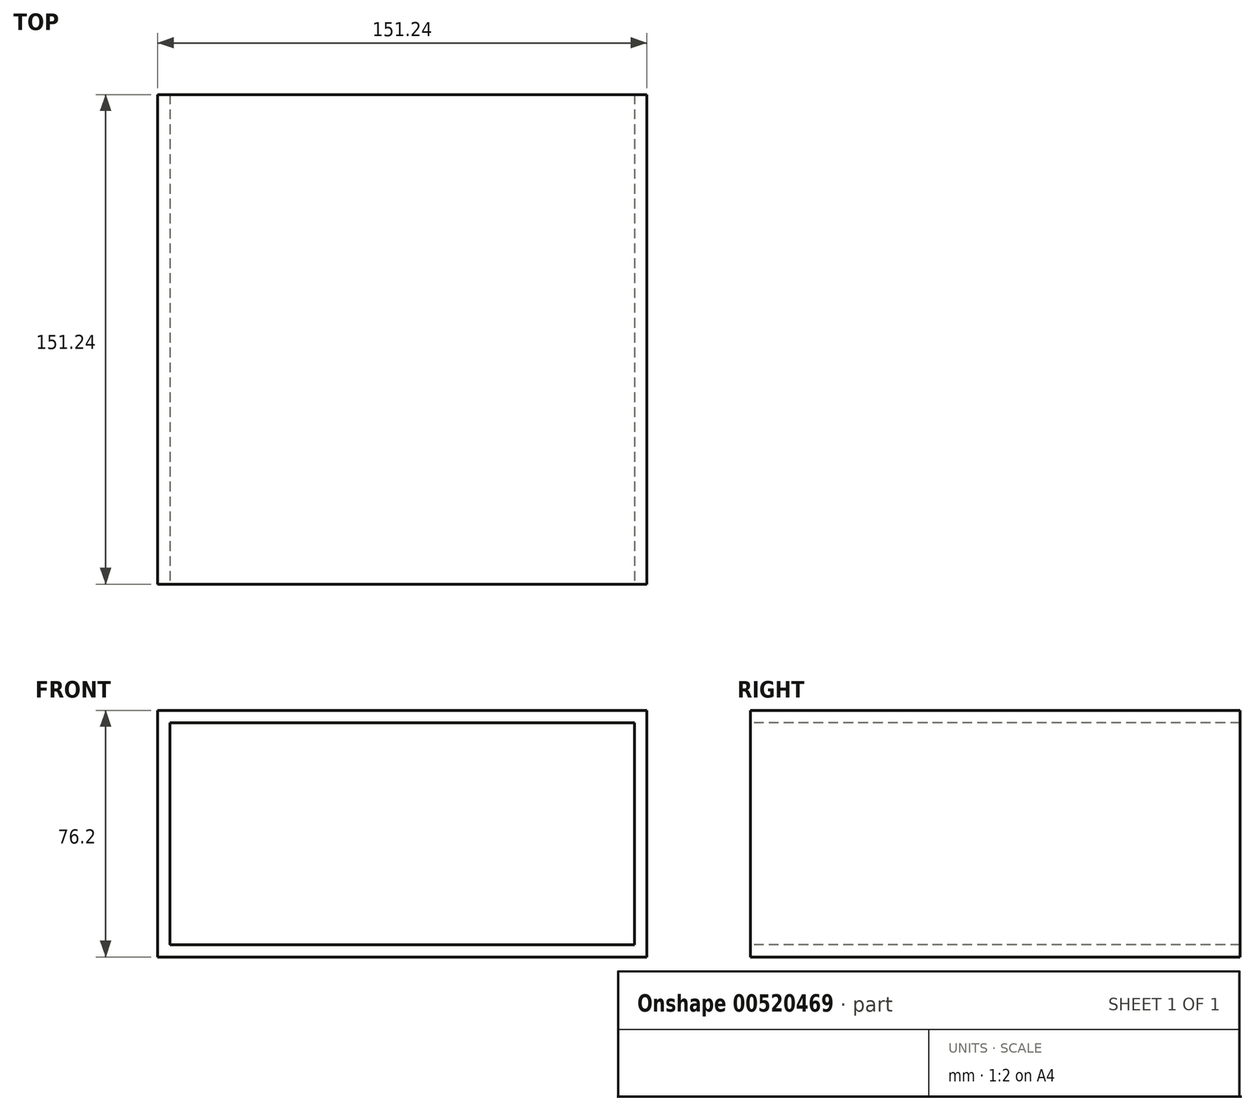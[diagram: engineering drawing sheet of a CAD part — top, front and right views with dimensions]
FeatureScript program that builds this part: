
annotation { "Feature Type Name" : "Feature", "Feature Type Description" : "" }
export const myFeature = defineFeature(function(context is Context, id is Id, definition is map)
    precondition{}
    {
        {
            var Q0;
            Q0=qCreatedBy(makeId("Top.planeOp"),FACE);
            var sketch = newSketch(context, id + "F0", { "sketchPlane" : qUnion([Q0])});
            skCircle(sketch, "E0.cCircle", {"center": v(0, 0) * mm, "radius": 75.62 * mm, "construction": true});
            skLineSegment(sketch, "E0.0", {"start": v(75.62, 75.62) * mm, "end": v(75.62, -75.62) * mm});
            skLineSegment(sketch, "E0.1", {"start": v(75.62, -75.62) * mm, "end": v(-75.62, -75.62) * mm});
            skLineSegment(sketch, "E0.2", {"start": v(-75.62, -75.62) * mm, "end": v(-75.62, 75.62) * mm});
            skLineSegment(sketch, "E0.3", {"start": v(-75.62, 75.62) * mm, "end": v(75.62, 75.62) * mm});
            skPoint(sketch, "E0.0.midPoint", {"position": v(75.62, 0) * mm});
            skSolve(sketch);
        }
        {
            var Q0;
            Q0 = qSketchRegion(id + "F0", true);
            extrude(context, id + "F1", {"entities" : qUnion([Q0]), "depth" : 76.2 * mm, "offsetDistance" : 25.4 * mm});
        }
        {
            var Q0;
            Q0=makeQuery(id+"F1.opExtrude","SWEPT_FACE",FACE,{"disambiguationData":[OSD([sQuery(id+"F0.wireOp",EDGE,"E0.1")])]});
            var sketch = newSketch(context, id + "F2", { "sketchPlane" : qUnion([Q0])});
            skLineSegment(sketch, "E1.bottom", {"start": v(-71.8, 72.4) * mm, "end": v(71.8, 72.4) * mm});
            skLineSegment(sketch, "E1.top", {"start": v(-71.8, 3.81) * mm, "end": v(71.8, 3.81) * mm});
            skLineSegment(sketch, "E1.left", {"start": v(-71.8, 72.4) * mm, "end": v(-71.8, 3.81) * mm});
            skLineSegment(sketch, "E1.right", {"start": v(71.8, 72.4) * mm, "end": v(71.8, 3.81) * mm});
            skSolve(sketch);
        }
        {
            var Q0;
            Q0 = qSketchRegion(id + "F2", true);
            extrude(context, id + "F3", {"entities" : qUnion([Q0]), "operationType" : NewBodyOperationType.REMOVE, "oppositeDirection" : true, "depth" : 151.38 * mm, "offsetDistance" : 25.4 * mm});
        }
    });
